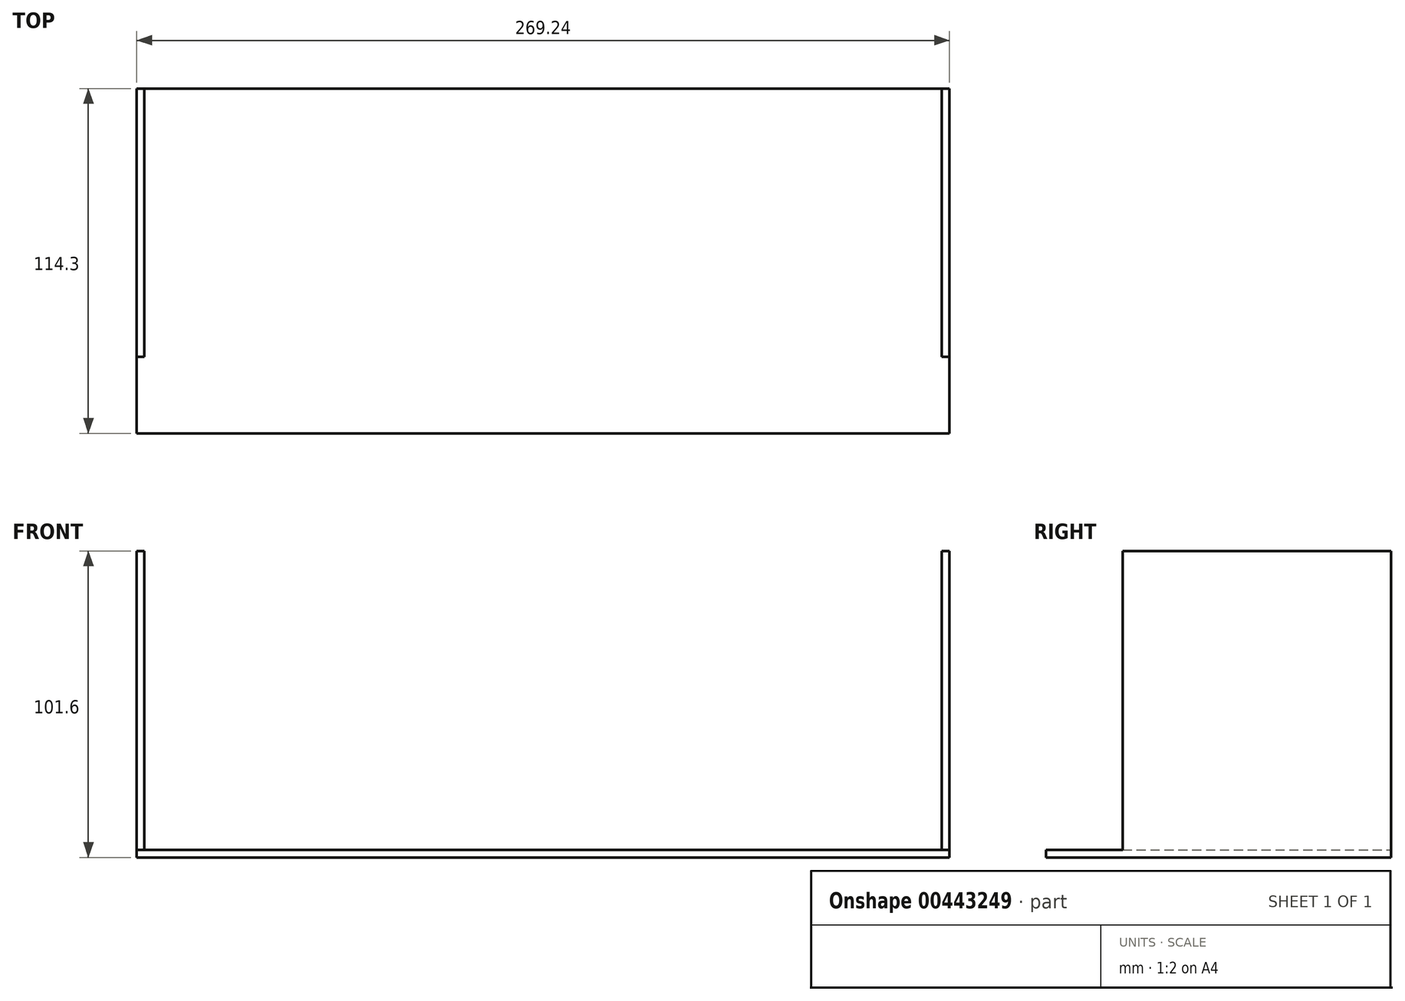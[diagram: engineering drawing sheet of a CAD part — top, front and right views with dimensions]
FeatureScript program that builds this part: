
annotation { "Feature Type Name" : "Feature", "Feature Type Description" : "" }
export const myFeature = defineFeature(function(context is Context, id is Id, definition is map)
    precondition{}
    {
        {
            var Q0;
            Q0=qCreatedBy(makeId("Front.planeOp"),FACE);
            var sketch = newSketch(context, id + "F0", { "sketchPlane" : qUnion([Q0])});
            skLineSegment(sketch, "E0.bottom", {"start": v(0, 0) * mm, "end": v(-264.16, 0) * mm});
            skLineSegment(sketch, "E0.top", {"start": v(0, 2.54) * mm, "end": v(-264.16, 2.54) * mm});
            skLineSegment(sketch, "E0.left", {"start": v(0, 0) * mm, "end": v(0, 2.54) * mm});
            skLineSegment(sketch, "E0.right", {"start": v(-264.16, 0) * mm, "end": v(-264.16, 2.54) * mm});
            skLineSegment(sketch, "E1.bottom", {"start": v(-264.16, 0) * mm, "end": v(-266.7, 0) * mm});
            skLineSegment(sketch, "E1.top", {"start": v(-264.16, 101.6) * mm, "end": v(-266.7, 101.6) * mm});
            skLineSegment(sketch, "E1.left", {"start": v(-264.16, 0) * mm, "end": v(-264.16, 101.6) * mm});
            skLineSegment(sketch, "E1.right", {"start": v(-266.7, 0) * mm, "end": v(-266.7, 101.6) * mm});
            skLineSegment(sketch, "E2.bottom", {"start": v(0, 0) * mm, "end": v(2.54, 0) * mm});
            skLineSegment(sketch, "E2.top", {"start": v(0, 101.6) * mm, "end": v(2.54, 101.6) * mm});
            skLineSegment(sketch, "E2.left", {"start": v(0, 0) * mm, "end": v(0, 101.6) * mm});
            skLineSegment(sketch, "E2.right", {"start": v(2.54, 0) * mm, "end": v(2.54, 101.6) * mm});
            skSolve(sketch);
        }
        {
            var Q0;
            Q0 = qSketchRegion(id + "F0", true);
            extrude(context, id + "F1", {"entities" : qUnion([Q0]), "depth" : 88.9 * mm});
        }
        {
            var Q0;
            Q0=makeQuery(id+"F1.opExtrude","CAP_FACE",FACE,{"disambiguationData":[OSD([sQuery(id+"F0.wireOp",EDGE,"E0.bottom"),sQuery(id+"F0.wireOp",EDGE,"E0.top"),sQuery(id+"F0.wireOp",EDGE,"E1.bottom"),sQuery(id+"F0.wireOp",EDGE,"E1.top"),sQuery(id+"F0.wireOp",EDGE,"E1.left"),sQuery(id+"F0.wireOp",EDGE,"E1.right"),sQuery(id+"F0.wireOp",EDGE,"E2.bottom"),sQuery(id+"F0.wireOp",EDGE,"E2.top"),sQuery(id+"F0.wireOp",EDGE,"E2.left"),sQuery(id+"F0.wireOp",EDGE,"E2.right")])],"isStart":true});
            var sketch = newSketch(context, id + "F2", { "sketchPlane" : qUnion([Q0])});
            skPoint(sketch, "E3.0", {"position": v(0, 2.54) * mm});
            skPoint(sketch, "E4.0", {"position": v(264.16, 2.54) * mm});
            skLineSegment(sketch, "E5", {"start": v(264.16, 2.54) * mm, "end": v(266.7, 2.54) * mm});
            skLineSegment(sketch, "E6", {"start": v(0, 2.54) * mm, "end": v(-2.54, 2.54) * mm});
            skSolve(sketch);
        }
        {
            var Q0;
            {var subQ2=sQuery(id+"F2.wireOp",EDGE,"E5");Q0=makeQuery(id+"F2.imprint","IMPRINT",FACE,{"disambiguationData":[TD([[makeQuery(id+"F2.imprint","IMPRINT",EDGE,{"derivedFrom":subQ2}),-1.0]])]});}
            extrude(context, id + "F3", {"entities" : qUnion([Q0]), "operationType" : NewBodyOperationType.ADD, "oppositeDirection" : true, "depth" : 114.3 * mm});
        }
    });
